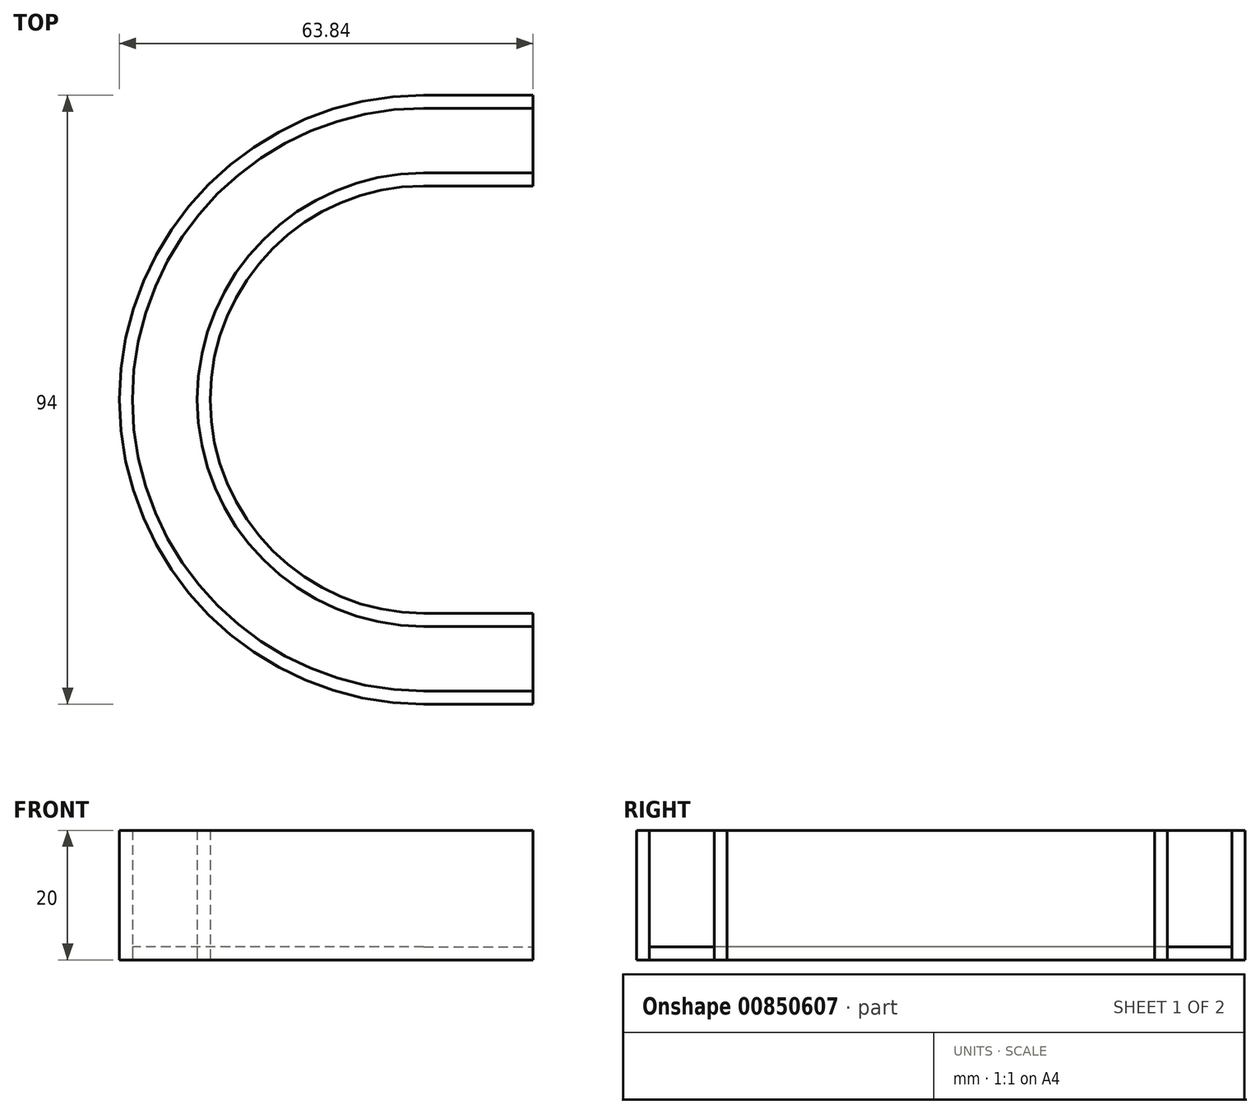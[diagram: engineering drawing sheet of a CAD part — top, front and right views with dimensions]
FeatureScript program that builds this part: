
annotation { "Feature Type Name" : "Feature", "Feature Type Description" : "" }
export const myFeature = defineFeature(function(context is Context, id is Id, definition is map)
    precondition{}
    {
        {
            var Q0;
            Q0=qCreatedBy(makeId("Top.planeOp"),FACE);
            var sketch = newSketch(context, id + "F0", { "sketchPlane" : qUnion([Q0])});
            skArc(sketch, "E0", {"start": v(0, 35) * mm, "mid": v(-24.75, 24.75) * mm, "end": v(-35, 0) * mm});
            skArc(sketch, "E1", {"start": v(0, 45) * mm, "mid": v(-31.82, 31.82) * mm, "end": v(-45, 0) * mm});
            skLineSegment(sketch, "E2", {"start": v(0, 45) * mm, "end": v(0, 35) * mm});
            skArc(sketch, "E3", {"start": v(0, 33) * mm, "mid": v(-23.33, 23.33) * mm, "end": v(-33, 0) * mm});
            skLineSegment(sketch, "E4", {"start": v(0, 35) * mm, "end": v(0, 33) * mm});
            skArc(sketch, "E5", {"start": v(0, 47) * mm, "mid": v(-33.23, 33.23) * mm, "end": v(-47, 0) * mm});
            skLineSegment(sketch, "E6", {"start": v(0, 47) * mm, "end": v(0, 33) * mm});
            skLineSegment(sketch, "E7.bottom", {"start": v(0, 47) * mm, "end": v(16.84, 47) * mm});
            skLineSegment(sketch, "E7.top", {"start": v(0, 45) * mm, "end": v(16.84, 45) * mm});
            skLineSegment(sketch, "E7.left", {"start": v(0, 47) * mm, "end": v(0, 45) * mm});
            skLineSegment(sketch, "E7.right", {"start": v(16.84, 47) * mm, "end": v(16.84, 45) * mm});
            skLineSegment(sketch, "E8.bottom", {"start": v(0, 35) * mm, "end": v(16.84, 35) * mm});
            skLineSegment(sketch, "E8.left", {"start": v(0, 35) * mm, "end": v(0, 45) * mm});
            skLineSegment(sketch, "E8.right", {"start": v(16.84, 35) * mm, "end": v(16.84, 45) * mm});
            skLineSegment(sketch, "E9.bottom", {"start": v(0, 33) * mm, "end": v(16.84, 33) * mm});
            skLineSegment(sketch, "E9.left", {"start": v(0, 33) * mm, "end": v(0, 35) * mm});
            skLineSegment(sketch, "E9.right", {"start": v(16.84, 33) * mm, "end": v(16.84, 35) * mm});
            skLineSegment(sketch, "E10", {"start": v(-47, 0) * mm, "end": v(-45, 0) * mm});
            skLineSegment(sketch, "E11", {"start": v(-45, 0) * mm, "end": v(0, 0) * mm});
            skLineSegment(sketch, "E12.MirrorCS", {"start": v(0, -35) * mm, "end": v(0, -33) * mm});
            skLineSegment(sketch, "E13.MirrorCS", {"start": v(0, -33) * mm, "end": v(0, -35) * mm});
            skLineSegment(sketch, "E14.MirrorCS", {"start": v(16.84, -33) * mm, "end": v(16.84, -35) * mm});
            skLineSegment(sketch, "E15.MirrorCS", {"start": v(0, -47) * mm, "end": v(0, -45) * mm});
            skLineSegment(sketch, "E16.MirrorCS", {"start": v(16.84, -47) * mm, "end": v(16.84, -45) * mm});
            skLineSegment(sketch, "E17.MirrorCS", {"start": v(0, -35) * mm, "end": v(16.84, -35) * mm});
            skLineSegment(sketch, "E18.MirrorCS", {"start": v(0, -45) * mm, "end": v(16.84, -45) * mm});
            skLineSegment(sketch, "E19.MirrorCS", {"start": v(0, -45) * mm, "end": v(0, -35) * mm});
            skLineSegment(sketch, "E20.MirrorCS", {"start": v(0, -47) * mm, "end": v(16.84, -47) * mm});
            skArc(sketch, "E21.MirrorCS", {"start": v(0, -35) * mm, "mid": v(-24.75, -24.75) * mm, "end": v(-35, 0) * mm});
            skArc(sketch, "E22.MirrorCS", {"start": v(0, -33) * mm, "mid": v(-23.33, -23.33) * mm, "end": v(-33, 0) * mm});
            skArc(sketch, "E23.MirrorCS", {"start": v(0, -47) * mm, "mid": v(-33.23, -33.23) * mm, "end": v(-47, 0) * mm});
            skLineSegment(sketch, "E24.MirrorCS", {"start": v(0, -35) * mm, "end": v(0, -45) * mm});
            skLineSegment(sketch, "E25.MirrorCS", {"start": v(16.84, -35) * mm, "end": v(16.84, -45) * mm});
            skLineSegment(sketch, "E26.MirrorCS", {"start": v(0, -33) * mm, "end": v(16.84, -33) * mm});
            skArc(sketch, "E27.MirrorCS", {"start": v(0, -45) * mm, "mid": v(-31.82, -31.82) * mm, "end": v(-45, 0) * mm});
            skLineSegment(sketch, "E28.MirrorCS", {"start": v(0, -47) * mm, "end": v(0, -33) * mm});
            skSolve(sketch);
        }
        {
            var Q0;
            Q0=makeQuery(id+"F0.imprint","IMPRINT",FACE,{"disambiguationData":[TD([[makeQuery(id+"F0.imprint","IMPRINT",EDGE,{"derivedFrom":sQuery(id+"F0.wireOp",EDGE,"E6")}),1.0]])]});
            var Q1;
            Q1=makeQuery(id+"F0.imprint","IMPRINT",FACE,{"disambiguationData":[TD([[makeQuery(id+"F0.imprint","IMPRINT",EDGE,{"derivedFrom":sQuery(id+"F0.wireOp",EDGE,"E4")}),1.0]])]});
            var Q2;
            Q2=makeQuery(id+"F0.imprint","IMPRINT",FACE,{"disambiguationData":[TD([[makeQuery(id+"F0.imprint","IMPRINT",EDGE,{"derivedFrom":sQuery(id+"F0.wireOp",EDGE,"E12.MirrorCS")}),-1.0]])]});
            var Q3;
            Q3=makeQuery(id+"F0.imprint","IMPRINT",FACE,{"disambiguationData":[TD([[makeQuery(id+"F0.imprint","IMPRINT",EDGE,{"derivedFrom":sQuery(id+"F0.wireOp",EDGE,"E15.MirrorCS")}),-1.0]])]});
            var Q4;
            {var subQ0=sQuery(id+"F0.wireOp",EDGE,"E0");Q4=makeQuery(id+"F0.imprint","IMPRINT",FACE,{"disambiguationData":[TD([[makeQuery(id+"F0.imprint","IMPRINT",EDGE,{"derivedFrom":subQ0}),1.0]])]});}
            var Q5;
            Q5=makeQuery(id+"F0.imprint","IMPRINT",FACE,{"disambiguationData":[TD([[makeQuery(id+"F0.imprint","IMPRINT",EDGE,{"derivedFrom":sQuery(id+"F0.wireOp",EDGE,"E1")}),-1.0]])]});
            var Q6;
            Q6=makeQuery(id+"F0.imprint","IMPRINT",FACE,{"disambiguationData":[TD([[makeQuery(id+"F0.imprint","IMPRINT",EDGE,{"derivedFrom":sQuery(id+"F0.wireOp",EDGE,"E12.MirrorCS")}),1.0]])]});
            var Q7;
            Q7=makeQuery(id+"F0.imprint","IMPRINT",FACE,{"disambiguationData":[TD([[makeQuery(id+"F0.imprint","IMPRINT",EDGE,{"derivedFrom":sQuery(id+"F0.wireOp",EDGE,"E10")}),-1.0]])]});
            extrude(context, id + "F1", {"entities" : qUnion([Q0, Q1, Q2, Q3, Q4, Q5, Q6, Q7]), "depth" : 20 * mm, "offsetDistance" : 25 * mm});
        }
        {
            var Q0;
            Q0=makeQuery(id+"F0.imprint","IMPRINT",FACE,{"disambiguationData":[TD([[makeQuery(id+"F0.imprint","IMPRINT",EDGE,{"derivedFrom":sQuery(id+"F0.wireOp",EDGE,"E19.MirrorCS")}),1.0]])]});
            var Q1;
            {var subQ0=sQuery(id+"F0.wireOp",EDGE,"E0");Q1=makeQuery(id+"F0.imprint","IMPRINT",FACE,{"disambiguationData":[TD([[makeQuery(id+"F0.imprint","IMPRINT",EDGE,{"derivedFrom":subQ0}),-1.0]])]});}
            var Q2;
            Q2=makeQuery(id+"F0.imprint","IMPRINT",FACE,{"disambiguationData":[TD([[makeQuery(id+"F0.imprint","IMPRINT",EDGE,{"derivedFrom":sQuery(id+"F0.wireOp",EDGE,"E2")}),1.0]])]});
            var Q3;
            Q3=makeQuery(id+"F0.imprint","IMPRINT",FACE,{"disambiguationData":[TD([[makeQuery(id+"F0.imprint","IMPRINT",EDGE,{"derivedFrom":sQuery(id+"F0.wireOp",EDGE,"E17.MirrorCS")}),-1.0]])]});
            extrude(context, id + "F2", {"entities" : qUnion([Q0, Q1, Q2, Q3]), "depth" : 2 * mm, "offsetDistance" : 25 * mm});
        }
    });
